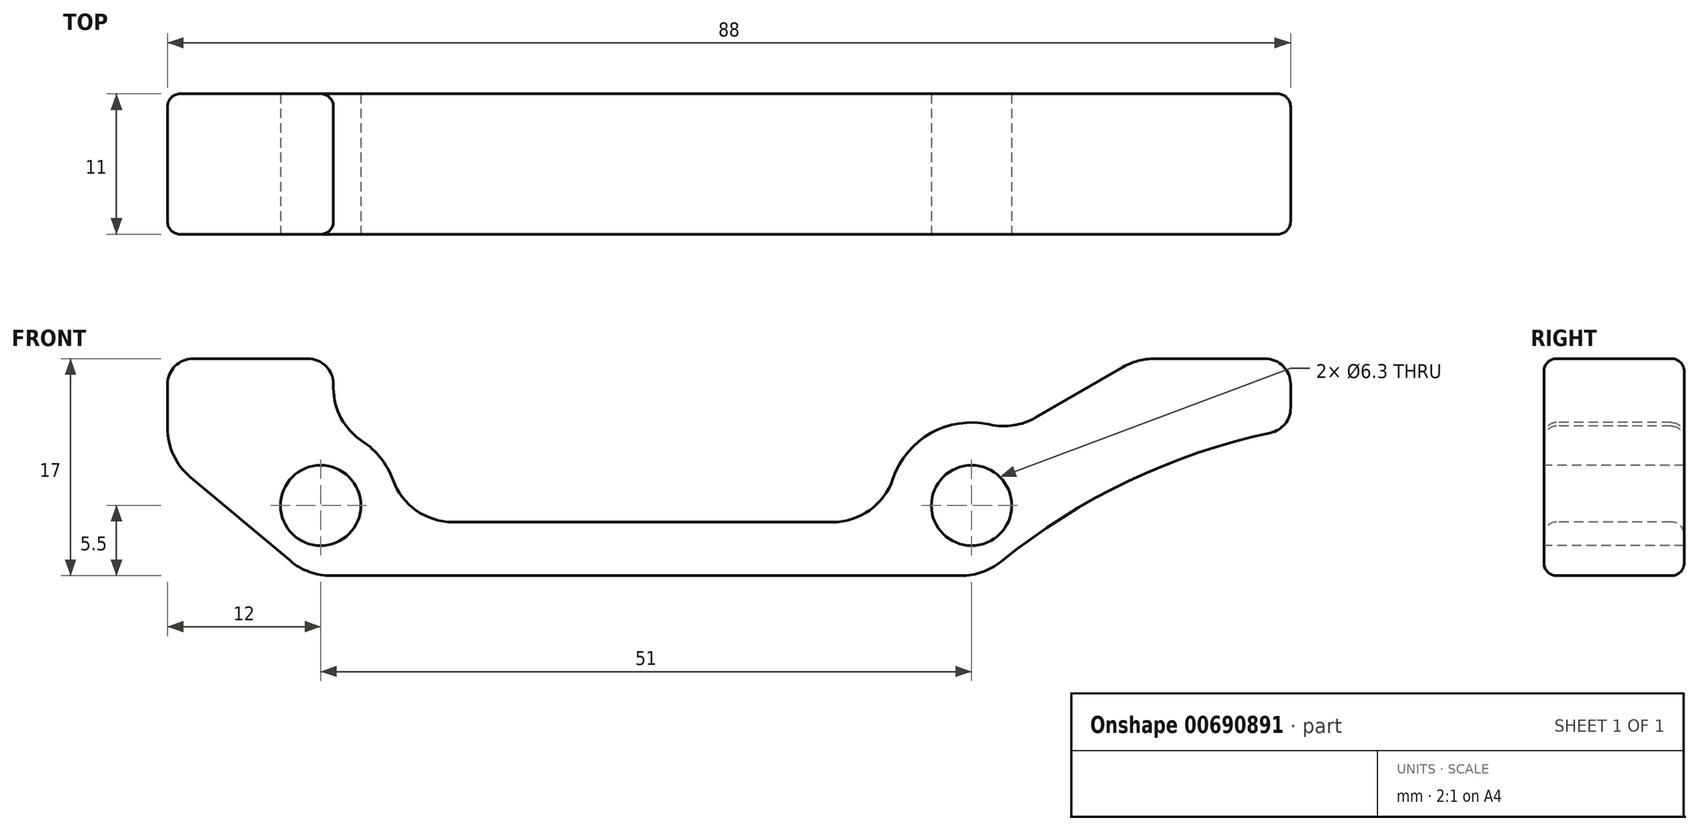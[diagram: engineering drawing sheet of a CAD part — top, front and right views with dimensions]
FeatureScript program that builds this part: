
annotation { "Feature Type Name" : "Feature", "Feature Type Description" : "" }
export const myFeature = defineFeature(function(context is Context, id is Id, definition is map)
    precondition{}
    {
        {
            var Q0;
            Q0=qCreatedBy(makeId("Front.planeOp"),FACE);
            var sketch = newSketch(context, id + "F0", { "sketchPlane" : qUnion([Q0])});
            skCircle(sketch, "E0", {"center": v(-25.5, 0) * mm, "radius": 3 * mm, "construction": true});
            skCircle(sketch, "E1", {"center": v(25.5, 0) * mm, "radius": 3 * mm, "construction": true});
            skLineSegment(sketch, "E2", {"start": v(-19.64, -1.3) * mm, "end": v(19.13, -1.3) * mm});
            skLineSegment(sketch, "E3", {"start": v(-25.5, 0) * mm, "end": v(25.5, 0) * mm, "construction": true});
            skLineSegment(sketch, "E4", {"start": v(-26.5, -5.5) * mm, "end": v(-37.5, 3.73) * mm});
            skLineSegment(sketch, "E5", {"start": v(-37.5, 3.73) * mm, "end": v(-37.5, 11.5) * mm});
            skLineSegment(sketch, "E6", {"start": v(-37.5, 11.5) * mm, "end": v(-24.5, 11.5) * mm});
            skArc(sketch, "E7", {"start": v(-19.64, -1.3) * mm, "mid": v(-20.52, 3.35) * mm, "end": v(-24.5, 5.92) * mm});
            skLineSegment(sketch, "E8", {"start": v(-24.5, 11.5) * mm, "end": v(-24.5, 5.92) * mm});
            skArc(sketch, "E9", {"start": v(28.54, 5.75) * mm, "mid": v(21.6, 5.2) * mm, "end": v(19.13, -1.3) * mm});
            skLineSegment(sketch, "E10", {"start": v(28.54, 5.75) * mm, "end": v(38.5, 11.5) * mm});
            skLineSegment(sketch, "E11", {"start": v(38.5, 11.5) * mm, "end": v(50.5, 11.5) * mm});
            skLineSegment(sketch, "E12", {"start": v(50.5, 11.5) * mm, "end": v(50.5, 6) * mm});
            skArc(sketch, "E13", {"start": v(50.5, 6) * mm, "mid": v(37.72, 1.88) * mm, "end": v(26.5, -5.5) * mm});
            skLineSegment(sketch, "E14", {"start": v(-26.5, -5.5) * mm, "end": v(26.5, -5.5) * mm});
            skLineSegment(sketch, "E15", {"start": v(0, -5.5) * mm, "end": v(0, 0) * mm, "construction": true});
            skSolve(sketch);
        }
        {
            var Q0;
            Q0 = qSketchRegion(id + "F0", true);
            extrude(context, id + "F1", {"entities" : qUnion([Q0]), "oppositeDirection" : true, "depth" : 11 * mm, "offsetDistance" : 25 * mm});
        }
        {
            var Q0;
            Q0=sQuery(id+"F0.wireOp",VERTEX,"E3.end");
            var Q1;
            Q1=sQuery(id+"F0.wireOp",VERTEX,"E3.start");
            var Q2;
            Q2=makeQuery(id+"F1.opExtrude","SWEPT_BODY",BODY,{"disambiguationData":[OSD([sQuery(id+"F0.wireOp",EDGE,"E2"),sQuery(id+"F0.wireOp",EDGE,"E4"),sQuery(id+"F0.wireOp",EDGE,"E5"),sQuery(id+"F0.wireOp",EDGE,"E6"),sQuery(id+"F0.wireOp",EDGE,"E7"),sQuery(id+"F0.wireOp",EDGE,"E8"),sQuery(id+"F0.wireOp",EDGE,"E9"),sQuery(id+"F0.wireOp",EDGE,"E10"),sQuery(id+"F0.wireOp",EDGE,"E11"),sQuery(id+"F0.wireOp",EDGE,"E12"),sQuery(id+"F0.wireOp",EDGE,"E13"),sQuery(id+"F0.wireOp",EDGE,"E14")])]});
            hole(context, id + "F2", {"style" : HoleStyle.SIMPLE, "endStyle" : HoleEndStyle.THROUGH, "standardTappedOrClearance" : lookupTablePath({ "standard" : "ISO", "fit" : "Close", "size" : "M6", "type" : "Clearance" }), "standardBlindInLast" : lookupTablePath({ "fit" : "Close", "standard" : "ISO", "size" : "M6", "type" : "Clearance" }), "holeDiameter" : 6.3 * mm, "majorDiameter" : 6 * mm, "isTappedThrough" : true, "tappedDepth" : 12 * mm, "tapClearance" : 3, "locations" : qUnion([Q0, Q1]), "scope" : qUnion([Q2])});
        }
        {
            var Q0;
            Q0=makeQuery(id+"F1.opExtrude","SWEPT_EDGE",EDGE,{"disambiguationData":[OSD([sQuery(id+"F0.wireOp",EDGE,"E7"),sQuery(id+"F0.wireOp",EDGE,"E8")])]});
            var Q1;
            Q1=makeQuery(id+"F1.opExtrude","SWEPT_EDGE",EDGE,{"disambiguationData":[OSD([sQuery(id+"F0.wireOp",EDGE,"E2"),sQuery(id+"F0.wireOp",EDGE,"E7")])]});
            var Q2;
            Q2=makeQuery(id+"F1.opExtrude","SWEPT_EDGE",EDGE,{"disambiguationData":[OSD([sQuery(id+"F0.wireOp",EDGE,"E2"),sQuery(id+"F0.wireOp",EDGE,"E9")])]});
            var Q3;
            Q3=makeQuery(id+"F1.opExtrude","SWEPT_EDGE",EDGE,{"disambiguationData":[OSD([sQuery(id+"F0.wireOp",EDGE,"E9"),sQuery(id+"F0.wireOp",EDGE,"E10")])]});
            var Q4;
            Q4=makeQuery(id+"F1.opExtrude","SWEPT_EDGE",EDGE,{"disambiguationData":[OSD([sQuery(id+"F0.wireOp",EDGE,"E4"),sQuery(id+"F0.wireOp",EDGE,"E5")])]});
            var Q5;
            Q5=makeQuery(id+"F1.opExtrude","SWEPT_EDGE",EDGE,{"disambiguationData":[OSD([sQuery(id+"F0.wireOp",EDGE,"E4"),sQuery(id+"F0.wireOp",EDGE,"E14")])]});
            var Q6;
            Q6=makeQuery(id+"F1.opExtrude","SWEPT_EDGE",EDGE,{"disambiguationData":[OSD([sQuery(id+"F0.wireOp",EDGE,"E13"),sQuery(id+"F0.wireOp",EDGE,"E14")])]});
            var Q7;
            Q7=makeQuery(id+"F1.opExtrude","SWEPT_EDGE",EDGE,{"disambiguationData":[OSD([sQuery(id+"F0.wireOp",EDGE,"E10"),sQuery(id+"F0.wireOp",EDGE,"E11")])]});
            fillet(context, id + "F3", {"entities" : qUnion([Q0, Q1, Q2, Q3, Q4, Q5, Q6, Q7]), "radius" : 5 * mm, "tangentPropagation" : true, "allowEdgeOverflow" : false});
        }
        {
            var Q0;
            Q0=makeQuery(id+"F1.opExtrude","SWEPT_EDGE",EDGE,{"disambiguationData":[OSD([sQuery(id+"F0.wireOp",EDGE,"E6"),sQuery(id+"F0.wireOp",EDGE,"E8")])]});
            var Q1;
            Q1=makeQuery(id+"F1.opExtrude","SWEPT_EDGE",EDGE,{"disambiguationData":[OSD([sQuery(id+"F0.wireOp",EDGE,"E5"),sQuery(id+"F0.wireOp",EDGE,"E6")])]});
            var Q2;
            Q2=makeQuery(id+"F1.opExtrude","SWEPT_EDGE",EDGE,{"disambiguationData":[OSD([sQuery(id+"F0.wireOp",EDGE,"E11"),sQuery(id+"F0.wireOp",EDGE,"E12")])]});
            var Q3;
            Q3=makeQuery(id+"F1.opExtrude","SWEPT_EDGE",EDGE,{"disambiguationData":[OSD([sQuery(id+"F0.wireOp",EDGE,"E12"),sQuery(id+"F0.wireOp",EDGE,"E13")])]});
            fillet(context, id + "F4", {"entities" : qUnion([Q0, Q1, Q2, Q3]), "radius" : 2 * mm, "tangentPropagation" : true, "allowEdgeOverflow" : false});
        }
        {
            var Q0;
            {var subQ0=sQuery(id+"F0.wireOp",EDGE,"E10");var subQ1=sQuery(id+"F0.wireOp",EDGE,"E9");Q0=makeQuery(id+"F3.opFillet","BLEND_EDGE",EDGE,{"blendedFrom":[makeQuery(id+"F1.opExtrude","SWEPT_EDGE",EDGE,{"disambiguationData":[OSD([subQ1,subQ0])]}),makeQuery(id+"F1.opExtrude","CAP_FACE",FACE,{"disambiguationData":[OSD([sQuery(id+"F0.wireOp",EDGE,"E2"),sQuery(id+"F0.wireOp",EDGE,"E4"),sQuery(id+"F0.wireOp",EDGE,"E5"),sQuery(id+"F0.wireOp",EDGE,"E6"),sQuery(id+"F0.wireOp",EDGE,"E7"),sQuery(id+"F0.wireOp",EDGE,"E8"),subQ1,subQ0,sQuery(id+"F0.wireOp",EDGE,"E11"),sQuery(id+"F0.wireOp",EDGE,"E12"),sQuery(id+"F0.wireOp",EDGE,"E13"),sQuery(id+"F0.wireOp",EDGE,"E14")])],"isStart":false})],"blendedInto":[makeQuery(id+"F1.opExtrude","CAP_FACE",FACE,{"disambiguationData":[OSD([sQuery(id+"F0.wireOp",EDGE,"E2"),sQuery(id+"F0.wireOp",EDGE,"E4"),sQuery(id+"F0.wireOp",EDGE,"E5"),sQuery(id+"F0.wireOp",EDGE,"E6"),sQuery(id+"F0.wireOp",EDGE,"E7"),sQuery(id+"F0.wireOp",EDGE,"E8"),subQ1,subQ0,sQuery(id+"F0.wireOp",EDGE,"E11"),sQuery(id+"F0.wireOp",EDGE,"E12"),sQuery(id+"F0.wireOp",EDGE,"E13"),sQuery(id+"F0.wireOp",EDGE,"E14")])],"isStart":false})]});}
            var Q1;
            Q1=makeQuery(id+"F1.opExtrude","CAP_EDGE",EDGE,{"disambiguationData":[OSD([sQuery(id+"F0.wireOp",EDGE,"E2")])],"isStart":true});
            fillet(context, id + "F5", {"entities" : qUnion([Q0, Q1]), "radius" : 1 * mm, "tangentPropagation" : true, "allowEdgeOverflow" : false});
        }
    });
